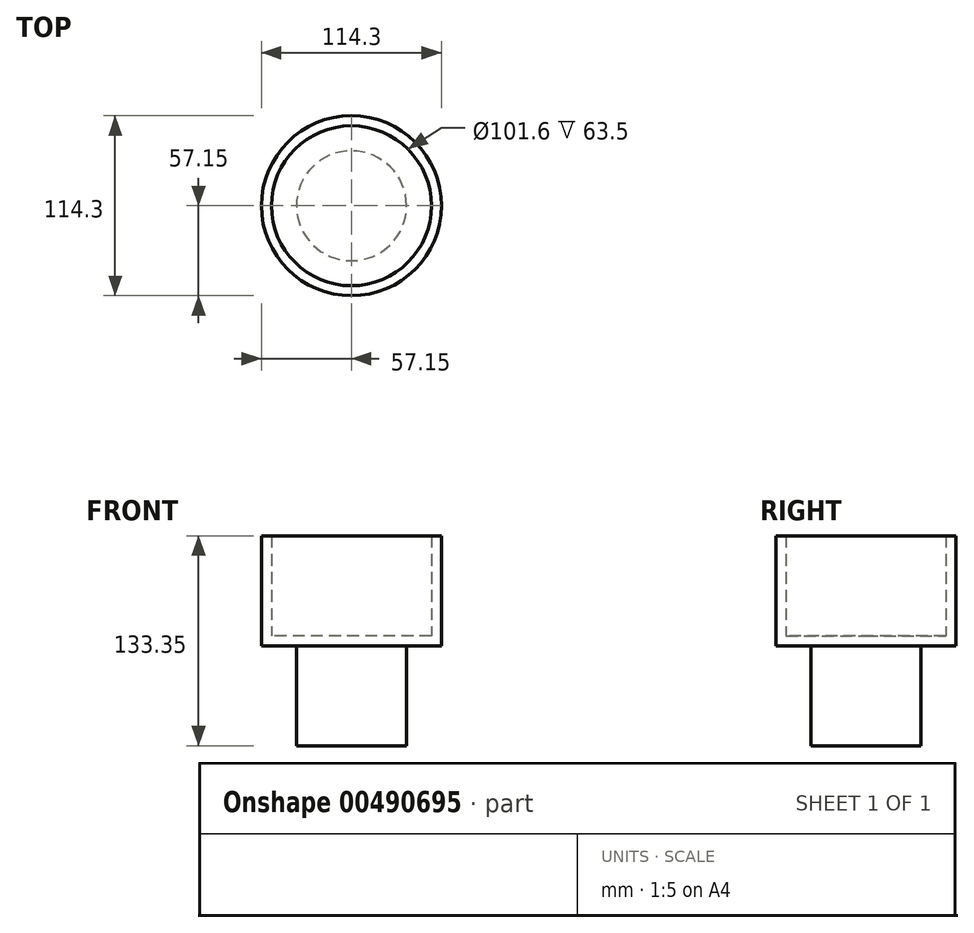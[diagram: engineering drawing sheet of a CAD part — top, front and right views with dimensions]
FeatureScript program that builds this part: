
annotation { "Feature Type Name" : "Feature", "Feature Type Description" : "" }
export const myFeature = defineFeature(function(context is Context, id is Id, definition is map)
    precondition{}
    {
        {
            var Q0;
            Q0=qCreatedBy(makeId("Top.planeOp"),FACE);
            var sketch = newSketch(context, id + "F0", { "sketchPlane" : qUnion([Q0])});
            skCircle(sketch, "E0", {"center": v(0, 0) * mm, "radius": 34.93 * mm});
            skSolve(sketch);
        }
        {
            var Q0;
            Q0=makeQuery(id+"F0.imprint","IMPRINT",FACE,{"disambiguationData":[TD([[makeQuery(id+"F0.imprint","IMPRINT",EDGE,{"derivedFrom":sQuery(id+"F0.wireOp",EDGE,"E0")}),1.0]])]});
            extrude(context, id + "F1", {"entities" : qUnion([Q0]), "depth" : 63.5 * mm});
        }
        {
            var Q0;
            Q0=makeQuery(id+"F1.opExtrude","CAP_FACE",FACE,{"disambiguationData":[OSD([sQuery(id+"F0.wireOp",EDGE,"E0")])],"isStart":false});
            var sketch = newSketch(context, id + "F2", { "sketchPlane" : qUnion([Q0])});
            skCircle(sketch, "E1", {"center": v(0, 0) * mm, "radius": 57.15 * mm});
            skSolve(sketch);
        }
        {
            var Q0;
            Q0=makeQuery(id+"F2.imprint","IMPRINT",FACE,{"disambiguationData":[TD([[makeQuery(id+"F2.imprint","IMPRINT",EDGE,{"derivedFrom":sQuery(id+"F2.wireOp",EDGE,"E1")}),1.0]])]});
            var Q1;
            Q1=makeQuery(id+"F2.imprint","IMPRINT",FACE,{"disambiguationData":[TD([[makeQuery(id+"F2.imprint","IMPRINT",EDGE,{"derivedFrom":makeQuery(id+"F1.opExtrude","CAP_EDGE",EDGE,{"disambiguationData":[OSD([sQuery(id+"F0.wireOp",EDGE,"E0")])],"isStart":false})}),1.0]])]});
            extrude(context, id + "F3", {"entities" : qUnion([Q0, Q1]), "operationType" : NewBodyOperationType.ADD, "depth" : 6.35 * mm});
        }
        {
            var Q0;
            Q0=makeQuery(id+"F3.opExtrude","CAP_FACE",FACE,{"disambiguationData":[OSD([sQuery(id+"F2.wireOp",EDGE,"E1")])],"isStart":false});
            var sketch = newSketch(context, id + "F4", { "sketchPlane" : qUnion([Q0])});
            skCircle(sketch, "E2", {"center": v(0, 0) * mm, "radius": 57.15 * mm});
            skCircle(sketch, "E3", {"center": v(0, 0) * mm, "radius": 50.8 * mm});
            skSolve(sketch);
        }
        {
            var Q0;
            Q0=makeQuery(id+"F4.imprint","IMPRINT",FACE,{"disambiguationData":[TD([[makeQuery(id+"F4.imprint","IMPRINT",EDGE,{"derivedFrom":sQuery(id+"F4.wireOp",EDGE,"E2")}),1.0]])]});
            extrude(context, id + "F5", {"entities" : qUnion([Q0]), "operationType" : NewBodyOperationType.ADD, "depth" : 63.5 * mm});
        }
    });
